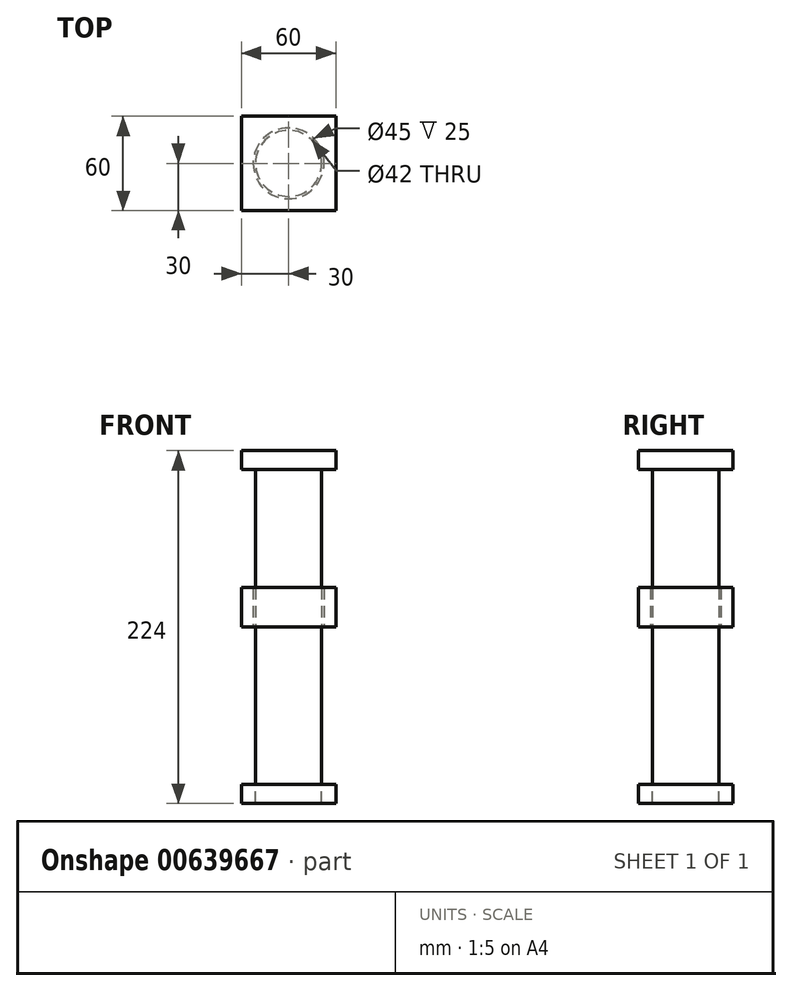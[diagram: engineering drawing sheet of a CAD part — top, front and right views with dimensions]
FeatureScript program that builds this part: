
annotation { "Feature Type Name" : "Feature", "Feature Type Description" : "" }
export const myFeature = defineFeature(function(context is Context, id is Id, definition is map)
    precondition{}
    {
        {
            var Q0;
            Q0=qCreatedBy(makeId("Top.planeOp"),FACE);
            var sketch = newSketch(context, id + "F0", { "sketchPlane" : qUnion([Q0])});
            skLineSegment(sketch, "E0.bottom", {"start": v(30, -30) * mm, "end": v(-30, -30) * mm});
            skLineSegment(sketch, "E0.top", {"start": v(30, 30) * mm, "end": v(-30, 30) * mm});
            skLineSegment(sketch, "E0.left", {"start": v(30, -30) * mm, "end": v(30, 30) * mm});
            skLineSegment(sketch, "E0.right", {"start": v(-30, -30) * mm, "end": v(-30, 30) * mm});
            skPoint(sketch, "E0.middle", {"position": v(0, 0) * mm});
            skSolve(sketch);
        }
        {
            var Q0;
            Q0=qCreatedBy(makeId("Top.planeOp"),FACE);
            var sketch = newSketch(context, id + "F1", { "sketchPlane" : qUnion([Q0])});
            skCircle(sketch, "E1", {"center": v(0, 0) * mm, "radius": 22.5 * mm});
            skSolve(sketch);
        }
        {
            var Q0;
            Q0=makeQuery(id+"F0.imprint","IMPRINT",FACE,{"disambiguationData":[TD([[makeQuery(id+"F0.imprint","IMPRINT",EDGE,{"derivedFrom":sQuery(id+"F0.wireOp",EDGE,"E0.bottom")}),-1.0]])]});
            extrude(context, id + "F2", {"entities" : qUnion([Q0]), "depth" : 25 * mm, "offsetDistance" : 25 * mm});
        }
        {
            var Q0;
            Q0 = qSketchRegion(id + "F1", true);
            extrude(context, id + "F3", {"entities" : qUnion([Q0]), "operationType" : NewBodyOperationType.REMOVE, "depth" : 25 * mm, "offsetDistance" : 25 * mm});
        }
        {
            var Q0;
            Q0=qCreatedBy(makeId("Top.planeOp"),FACE);
            var sketch = newSketch(context, id + "F4", { "sketchPlane" : qUnion([Q0])});
            skCircle(sketch, "E2", {"center": v(0, 0) * mm, "radius": 21 * mm});
            skSolve(sketch);
        }
        {
            var Q0;
            Q0=makeQuery(id+"F4.imprint","IMPRINT",FACE,{"disambiguationData":[TD([[makeQuery(id+"F4.imprint","IMPRINT",EDGE,{"derivedFrom":sQuery(id+"F4.wireOp",EDGE,"E2")}),1.0]])]});
            extrude(context, id + "F5", {"entities" : qUnion([Q0]), "endBound" : BoundingType.SYMMETRIC, "depth" : 200 * mm, "offsetDistance" : 25 * mm});
        }
        {
            var Q0;
            Q0=makeQuery(id+"F5.opExtrude","CAP_FACE",FACE,{"disambiguationData":[OSD([sQuery(id+"F4.wireOp",EDGE,"E2")])],"isStart":false});
            var sketch = newSketch(context, id + "F6", { "sketchPlane" : qUnion([Q0])});
            skLineSegment(sketch, "E3.bottom", {"start": v(30, 30) * mm, "end": v(-30, 30) * mm});
            skLineSegment(sketch, "E3.top", {"start": v(30, -30) * mm, "end": v(-30, -30) * mm});
            skLineSegment(sketch, "E3.left", {"start": v(30, 30) * mm, "end": v(30, -30) * mm});
            skLineSegment(sketch, "E3.right", {"start": v(-30, 30) * mm, "end": v(-30, -30) * mm});
            skPoint(sketch, "E3.middle", {"position": v(0, 0) * mm});
            skSolve(sketch);
        }
        {
            var Q0;
            Q0 = qSketchRegion(id + "F6", true);
            extrude(context, id + "F7", {"entities" : qUnion([Q0]), "operationType" : NewBodyOperationType.ADD, "depth" : 12 * mm, "offsetDistance" : 25 * mm});
        }
        {
            var Q0;
            Q0=makeQuery(id+"F5.opExtrude","CAP_FACE",FACE,{"disambiguationData":[OSD([sQuery(id+"F4.wireOp",EDGE,"E2")])],"isStart":true});
            var sketch = newSketch(context, id + "F8", { "sketchPlane" : qUnion([Q0])});
            skSolve(sketch);
        }
        {
            var Q0;
            Q0=makeQuery(id+"F8.imprint","IMPRINT",FACE,{"disambiguationData":[TD([[makeQuery(id+"F8.imprint","IMPRINT",EDGE,{"derivedFrom":makeQuery(id+"F5.opExtrude","CAP_EDGE",EDGE,{"disambiguationData":[OSD([sQuery(id+"F4.wireOp",EDGE,"E2")])],"isStart":true})}),-1.0]])]});
            var sketch = newSketch(context, id + "F9", { "sketchPlane" : qUnion([Q0])});
            skLineSegment(sketch, "E4.bottom", {"start": v(-30, 30) * mm, "end": v(30, 30) * mm});
            skLineSegment(sketch, "E4.top", {"start": v(-30, -30) * mm, "end": v(30, -30) * mm});
            skLineSegment(sketch, "E4.left", {"start": v(-30, 30) * mm, "end": v(-30, -30) * mm});
            skLineSegment(sketch, "E4.right", {"start": v(30, 30) * mm, "end": v(30, -30) * mm});
            skPoint(sketch, "E4.middle", {"position": v(0, 0) * mm});
            skSolve(sketch);
        }
        {
            var Q0;
            Q0=makeQuery(id+"F9.imprint","IMPRINT",FACE,{"disambiguationData":[TD([[makeQuery(id+"F9.imprint","IMPRINT",EDGE,{"derivedFrom":sQuery(id+"F9.wireOp",EDGE,"E4.bottom")}),-1.0]])]});
            extrude(context, id + "F10", {"entities" : qUnion([Q0]), "depth" : 12 * mm, "offsetDistance" : 25 * mm});
        }
    });
